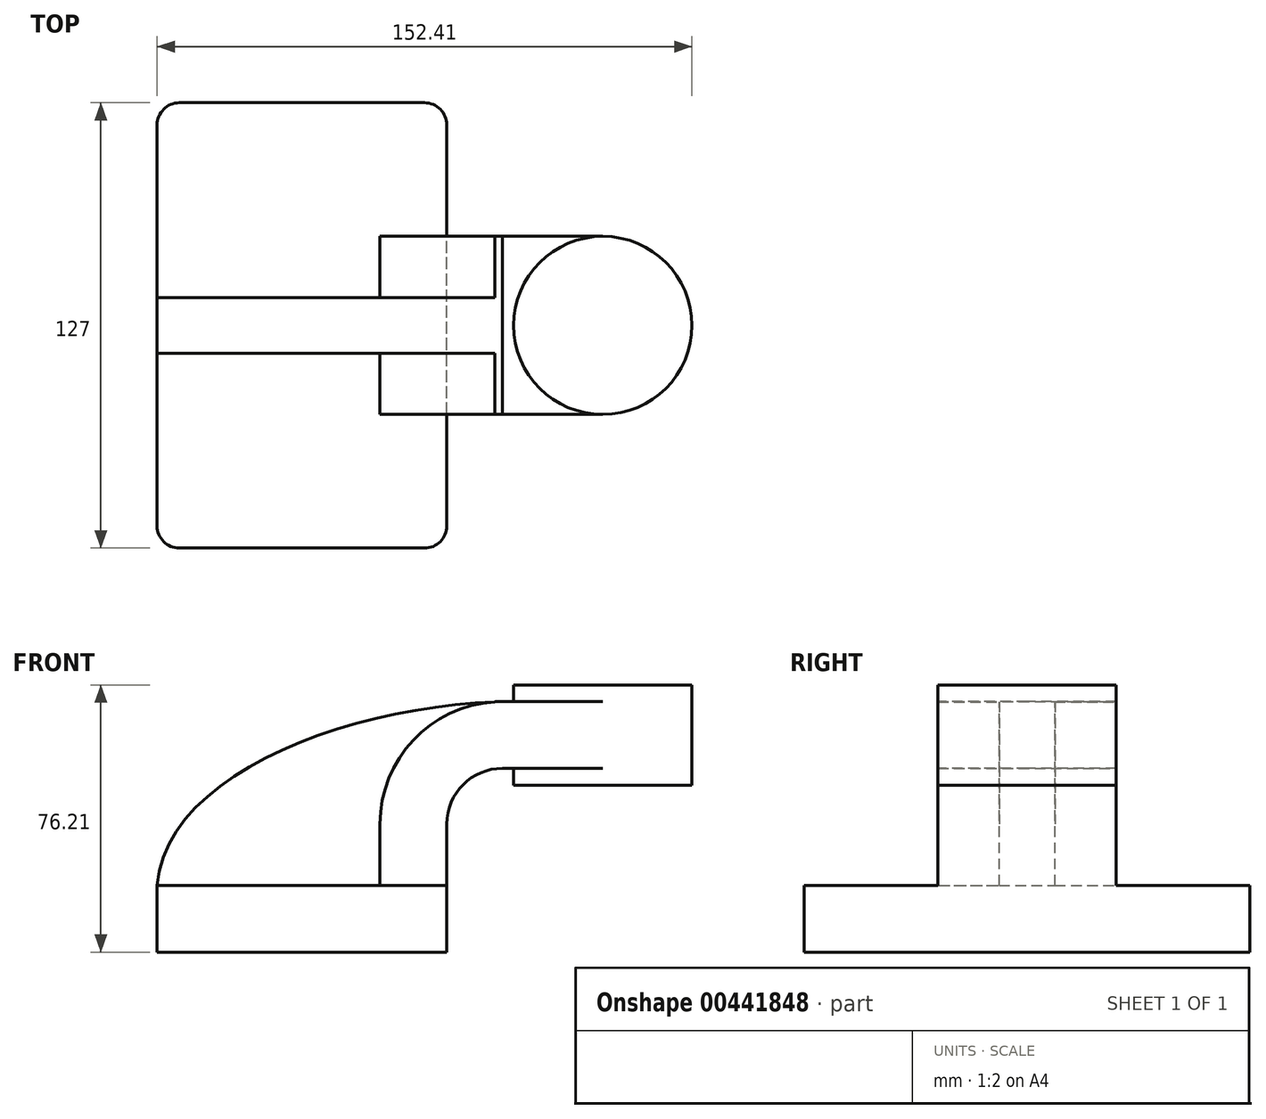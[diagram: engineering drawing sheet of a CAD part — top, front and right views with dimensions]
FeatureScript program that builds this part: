
annotation { "Feature Type Name" : "Feature", "Feature Type Description" : "" }
export const myFeature = defineFeature(function(context is Context, id is Id, definition is map)
    precondition{}
    {
        {
            var Q0;
            Q0=qCreatedBy(makeId("Front.planeOp"),FACE);
            var sketch = newSketch(context, id + "F0", { "sketchPlane" : qUnion([Q0])});
            skLineSegment(sketch, "E0.bottom", {"start": v(41.28, -9.52) * mm, "end": v(-41.27, -9.53) * mm});
            skLineSegment(sketch, "E0.top", {"start": v(41.27, 9.53) * mm, "end": v(-41.28, 9.53) * mm});
            skLineSegment(sketch, "E0.left", {"start": v(41.28, -9.52) * mm, "end": v(41.28, 9.53) * mm});
            skLineSegment(sketch, "E0.right", {"start": v(-41.27, -9.53) * mm, "end": v(-41.28, 9.53) * mm});
            skPoint(sketch, "E0.middle", {"position": v(0, 0) * mm});
            skLineSegment(sketch, "E1.bottom", {"start": v(60.32, 38.1) * mm, "end": v(111.12, 38.1) * mm});
            skLineSegment(sketch, "E1.top", {"start": v(60.32, 66.68) * mm, "end": v(111.12, 66.68) * mm});
            skLineSegment(sketch, "E1.left", {"start": v(60.32, 38.1) * mm, "end": v(60.32, 66.68) * mm});
            skLineSegment(sketch, "E1.right", {"start": v(111.12, 38.1) * mm, "end": v(111.12, 66.68) * mm});
            skPoint(sketch, "E1.middle", {"position": v(85.72, 52.39) * mm});
            skLineSegment(sketch, "E2", {"start": v(41.27, 9.53) * mm, "end": v(41.27, 27) * mm});
            skArc(sketch, "E3", {"start": v(41.27, 27) * mm, "mid": v(45.92, 38.23) * mm, "end": v(57.15, 42.88) * mm});
            skLineSegment(sketch, "E4", {"start": v(57.15, 42.88) * mm, "end": v(85.72, 42.88) * mm});
            skPoint(sketch, "E4.endSnap0", {"position": v(85.72, 38.1) * mm});
            skLineSegment(sketch, "E5.0", {"start": v(57.15, 61.93) * mm, "end": v(85.72, 61.93) * mm});
            skArc(sketch, "E5.1", {"start": v(22.23, 27) * mm, "mid": v(32.45, 51.7) * mm, "end": v(57.15, 61.93) * mm});
            skLineSegment(sketch, "E5.2", {"start": v(22.22, 9.53) * mm, "end": v(22.22, 27) * mm});
            skLineSegment(sketch, "E6", {"start": v(85.72, 38.1) * mm, "end": v(85.72, 66.68) * mm});
            skFitSpline(sketch, "E7", {"points": [v(-41.28, 9.52) * mm, v(57.15, 61.93) * mm], "startDerivative": vector(7.84, 96.75) * mm, "endDerivative": vector(128.09, 3.19) * mm});
            skSolve(sketch);
        }
        {
            var Q0;
            Q0=makeQuery(id+"F0.imprint","IMPRINT",FACE,{"disambiguationData":[TD([[makeQuery(id+"F0.imprint","IMPRINT",EDGE,{"derivedFrom":sQuery(id+"F0.wireOp",EDGE,"E0.bottom")}),-1.0]])]});
            extrude(context, id + "F1", {"entities" : qUnion([Q0]), "endBound" : BoundingType.SYMMETRIC, "depth" : 127 * mm});
        }
        {
            var Q0;
            {var subQ1=sQuery(id+"F0.wireOp",EDGE,"E2");Q0=makeQuery(id+"F0.imprint","IMPRINT",FACE,{"disambiguationData":[TD([[makeQuery(id+"F0.imprint","IMPRINT",EDGE,{"derivedFrom":subQ1}),1.0]])]});}
            extrude(context, id + "F2", {"entities" : qUnion([Q0]), "operationType" : NewBodyOperationType.ADD, "endBound" : BoundingType.SYMMETRIC, "depth" : 50.8 * mm});
        }
        {
            var Q0;
            {var subQ3=sQuery(id+"F0.wireOp",EDGE,"E5.2");Q0=makeQuery(id+"F0.imprint","IMPRINT",FACE,{"disambiguationData":[TD([[makeQuery(id+"F0.imprint","IMPRINT",EDGE,{"derivedFrom":subQ3}),1.0]])]});}
            extrude(context, id + "F3", {"entities" : qUnion([Q0]), "operationType" : NewBodyOperationType.ADD, "endBound" : BoundingType.SYMMETRIC, "depth" : 15.88 * mm});
        }
        {
            var Q0;
            {var subQ0=sQuery(id+"F0.wireOp",EDGE,"E4");var subQ1=sQuery(id+"F0.wireOp",EDGE,"E1.left");var subQ2=makeQuery(id+"F0.imprint","INTERSECT",VERTEX,{"derivedFrom":[subQ1,subQ0]});Q0=makeQuery(id+"F0.imprint","IMPRINT",FACE,{"disambiguationData":[TD([[makeQuery(id+"F0.imprint","IMPRINT",EDGE,{"disambiguationData":[TD([[subQ2,-1.0]])],"derivedFrom":subQ1}),-1.0]])]});}
            extrude(context, id + "F4", {"entities" : qUnion([Q0]), "operationType" : NewBodyOperationType.ADD, "endBound" : BoundingType.SYMMETRIC, "depth" : 50.8 * mm});
        }
        {
            var Q0;
            {var subQ4=sQuery(id+"F0.wireOp",EDGE,"E1.right");Q0=makeQuery(id+"F0.imprint","IMPRINT",FACE,{"disambiguationData":[TD([[makeQuery(id+"F0.imprint","IMPRINT",EDGE,{"derivedFrom":subQ4}),1.0]])]});}
            var Q1;
            Q1=sQuery(id+"F0.wireOp",EDGE,"E6");
            revolve(context, id + "F5", {"operationType" : NewBodyOperationType.ADD, "entities" : qUnion([Q0]), "axis" : qUnion([Q1]), "revolveType" : RevolveType.FULL});
        }
        {
            var Q0;
            Q0=makeQuery(id+"F1.opExtrude","CAP_EDGE",EDGE,{"disambiguationData":[OSD([sQuery(id+"F0.wireOp",EDGE,"E0.right")])],"isStart":false});
            var Q1;
            Q1=makeQuery(id+"F1.opExtrude","CAP_EDGE",EDGE,{"disambiguationData":[OSD([sQuery(id+"F0.wireOp",EDGE,"E0.left")])],"isStart":false});
            var Q2;
            Q2=makeQuery(id+"F1.opExtrude","CAP_EDGE",EDGE,{"disambiguationData":[OSD([sQuery(id+"F0.wireOp",EDGE,"E0.left")])],"isStart":true});
            var Q3;
            Q3=makeQuery(id+"F1.opExtrude","CAP_EDGE",EDGE,{"disambiguationData":[OSD([sQuery(id+"F0.wireOp",EDGE,"E0.right")])],"isStart":true});
            fillet(context, id + "F6", {"entities" : qUnion([Q0, Q1, Q2, Q3]), "radius" : 6.35 * mm, "tangentPropagation" : true, "allowEdgeOverflow" : false});
        }
    });
